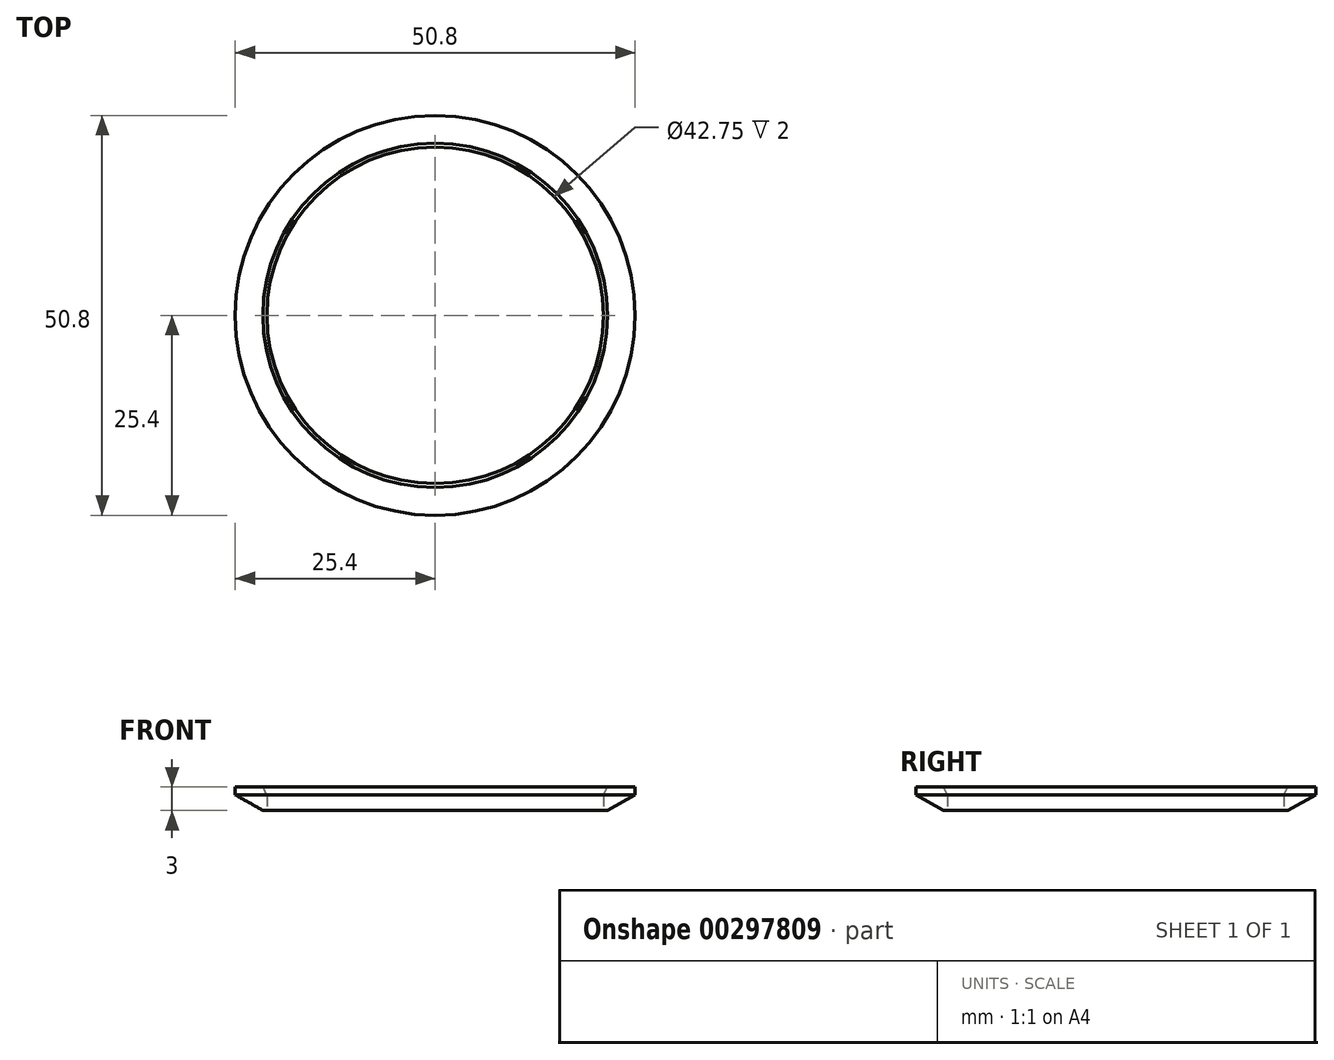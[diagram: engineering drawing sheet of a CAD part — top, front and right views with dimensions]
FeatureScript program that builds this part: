
annotation { "Feature Type Name" : "Feature", "Feature Type Description" : "" }
export const myFeature = defineFeature(function(context is Context, id is Id, definition is map)
    precondition{}
    {
        {
            var Q0;
            Q0=qCreatedBy(makeId("Front.planeOp"),FACE);
            var sketch = newSketch(context, id + "F0", { "sketchPlane" : qUnion([Q0])});
            skLineSegment(sketch, "E0", {"start": v(21.38, 2) * mm, "end": v(21.38, 0) * mm});
            skLineSegment(sketch, "E1", {"start": v(21.38, 0) * mm, "end": v(21.88, 0) * mm});
            skLineSegment(sketch, "E2", {"start": v(25.4, 2) * mm, "end": v(25.4, 3) * mm});
            skLineSegment(sketch, "E3", {"start": v(25.4, 3) * mm, "end": v(21.88, 3) * mm});
            skLineSegment(sketch, "E4", {"start": v(0, -6.56) * mm, "end": v(0, 19.86) * mm, "construction": true});
            skLineSegment(sketch, "E5", {"start": v(21.88, 0) * mm, "end": v(25.4, 2) * mm});
            skLineSegment(sketch, "E6", {"start": v(21.38, 2) * mm, "end": v(21.88, 3) * mm});
            skSolve(sketch);
        }
        {
            var Q0;
            Q0=makeQuery(id+"F0.imprint","IMPRINT",FACE,{"disambiguationData":[TD([[makeQuery(id+"F0.imprint","IMPRINT",EDGE,{"derivedFrom":sQuery(id+"F0.wireOp",EDGE,"E0")}),1.0]])]});
            var Q1;
            Q1=sQuery(id+"F0.wireOp",EDGE,"E4");
            revolve(context, id + "F1", {"entities" : qUnion([Q0]), "axis" : qUnion([Q1]), "revolveType" : RevolveType.FULL});
        }
    });
